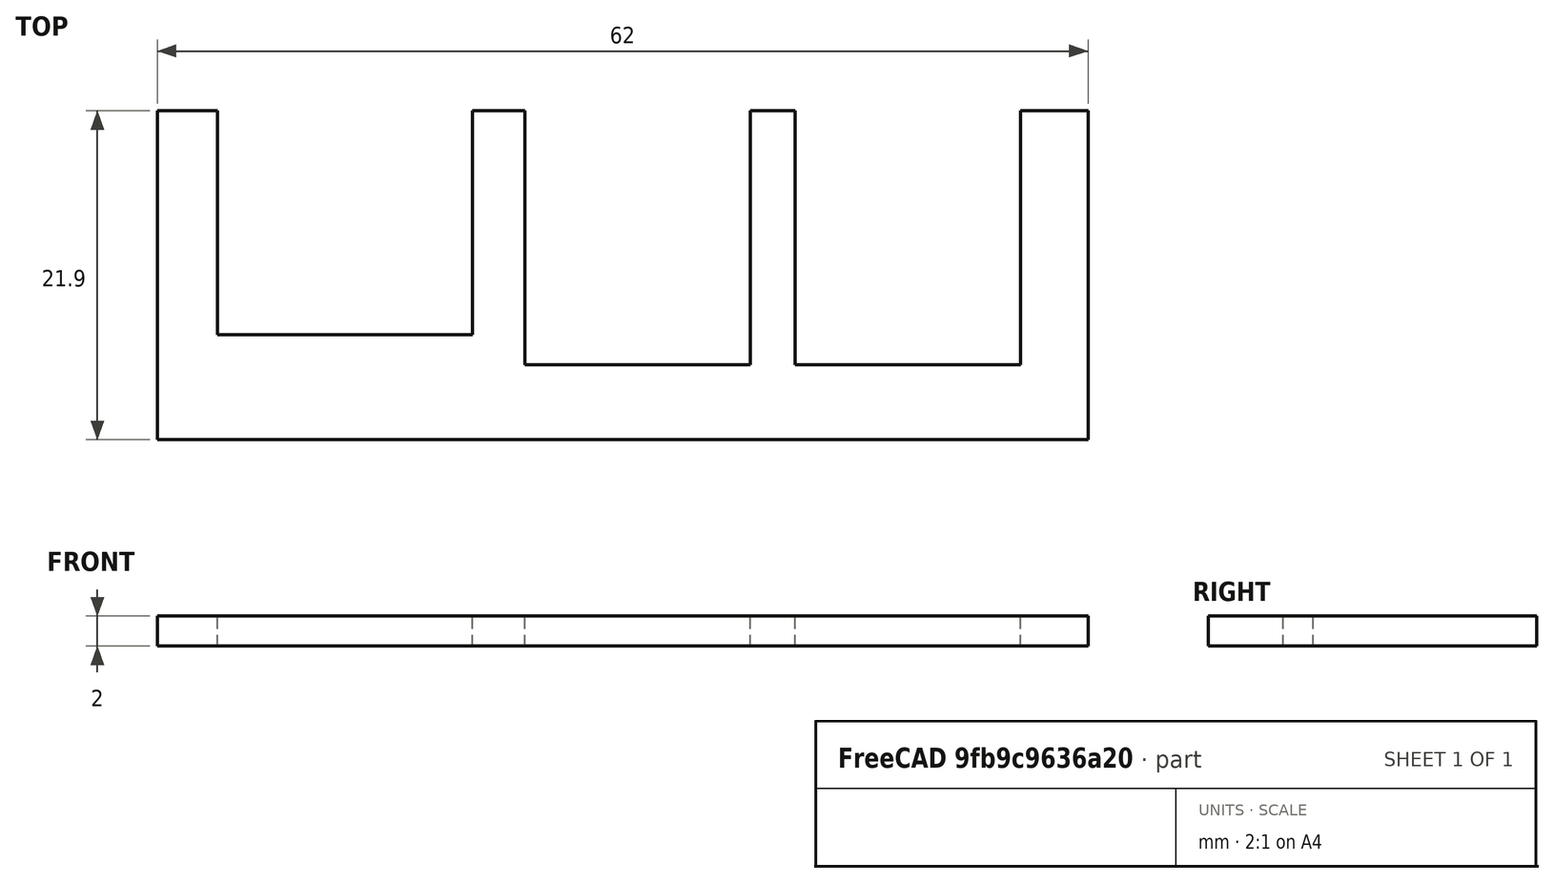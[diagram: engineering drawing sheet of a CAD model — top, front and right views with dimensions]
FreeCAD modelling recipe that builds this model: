
FCSTD DOCUMENT  (FreeCAD 0.19R23141 (Git))
Label: FacePlate
License: All rights reserved
LicenseURL: http://en.wikipedia.org/wiki/All_rights_reserved
objects: Sketcher::SketchObject×1, PartDesign::Pad×1, PartDesign::Body×1
note: 4 computed .brp shape members not serialized (recipe doc carries the construction recipe); baked Part::Feature solids carry a one-line shape summary decoded from their .brp

FEATURE [Sketcher::SketchObject] Sketch
  MapMode = 5
  Support = -> [XY_Plane]
  sketch-geometry (16):
    g0: LineSegment StartX=0 StartY=0 StartZ=0 EndX=62 EndY=0 EndZ=0
    g1: LineSegment StartX=0 StartY=0 StartZ=0 EndX=0 EndY=21.9 EndZ=0
    g2: LineSegment StartX=0 StartY=21.9 StartZ=0 EndX=4 EndY=21.9 EndZ=0
    g3: LineSegment StartX=4 StartY=21.9 StartZ=0 EndX=4 EndY=7 EndZ=0
    g4: LineSegment StartX=4 StartY=7 StartZ=0 EndX=21 EndY=7 EndZ=0
    g5: LineSegment StartX=21 StartY=7 StartZ=0 EndX=21 EndY=21.9 EndZ=0
    g6: LineSegment StartX=21 StartY=21.9 StartZ=0 EndX=24.5 EndY=21.9 EndZ=0
    g7: LineSegment StartX=24.5 StartY=21.9 StartZ=0 EndX=24.5 EndY=5 EndZ=0
    g8: LineSegment StartX=24.5 StartY=5 StartZ=0 EndX=39.5 EndY=5 EndZ=0
    g9: LineSegment StartX=39.5 StartY=5 StartZ=0 EndX=39.5 EndY=21.9 EndZ=0
    g10: LineSegment StartX=39.5 StartY=21.9 StartZ=0 EndX=42.5 EndY=21.9 EndZ=0
    g11: LineSegment StartX=42.5 StartY=21.9 StartZ=0 EndX=42.5 EndY=5 EndZ=0
    g12: LineSegment StartX=42.5 StartY=5 StartZ=0 EndX=57.5 EndY=5 EndZ=0
    g13: LineSegment StartX=57.5 StartY=5 StartZ=0 EndX=57.5 EndY=21.9 EndZ=0
    g14: LineSegment StartX=57.5 StartY=21.9 StartZ=0 EndX=62 EndY=21.9 EndZ=0
    g15: LineSegment StartX=62 StartY=21.9 StartZ=0 EndX=62 EndY=0 EndZ=0
  constraints (47):
    c: Coincident(g0,g-1)
    c: PointOnObject(g0,g-1)
    c: DistanceX(g0,g0) = 62
    c: Coincident(g1,g0)
    c: PointOnObject(g1,g-2)
    c: DistanceY(g1,g1) = 21.9
    c: Coincident(g2,g1)
    c: Horizontal(g2)
    c: DistanceX(g2,g2) = 4
    c: Coincident(g3,g2)
    c: Vertical(g3)
    c: Coincident(g4,g3)
    c: Horizontal(g4)
    c: DistanceX(g0,g4) = 21
    c: DistanceY(g0,g3) = 7
    c: Coincident(g5,g4)
    c: Vertical(g5)
    c: DistanceY(g0,g5) = 21.9
    c: Coincident(g6,g5)
    c: DistanceX(g6,g6) = 3.5
    c: Coincident(g7,g6)
    c: Vertical(g7)
    c: DistanceY(g0,g7) = 5
    c: DistanceY(g0,g6) = 21.9
    c: Coincident(g8,g7)
    c: Horizontal(g8)
    c: DistanceX(g8,g8) = 15
    c: Coincident(g9,g8)
    c: Vertical(g9)
    c: DistanceY(g0,g9) = 21.9
    c: Coincident(g10,g9)
    c: Horizontal(g10)
    c: DistanceX(g10,g10) = 3
    c: Coincident(g11,g10)
    c: Vertical(g11)
    c: DistanceY(g0,g11) = 5
    c: Coincident(g12,g11)
    c: Horizontal(g12)
    c: DistanceX(g12,g12) = 15
    c: Coincident(g13,g12)
    c: Vertical(g13)
    c: Coincident(g14,g13)
    c: DistanceX(g14,g14) = 4.5
    c: Coincident(g15,g14)
    c: Coincident(g15,g0)
    c: DistanceY(g15,g15) = 21.9
    c: DistanceY(g0,g13) = 21.9
FEATURE [PartDesign::Pad] Pad
  Direction = (1,1,1)
  Length = 2
  Length2 = 100
  Profile = -> Sketch
  Type = 0
FEATURE [PartDesign::Body] Body
  Group = -> [Sketch,Pad]
  Origin = -> Origin
  Tip = -> Pad
